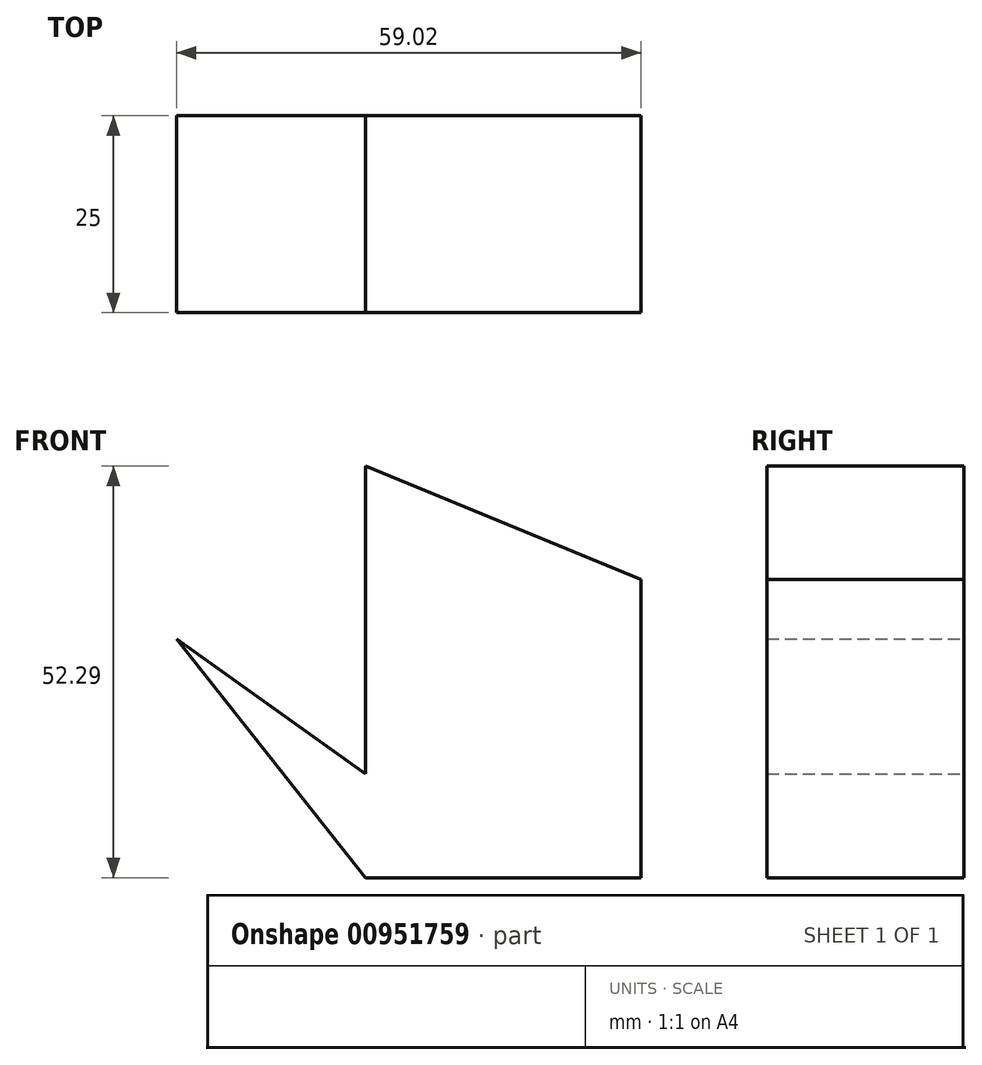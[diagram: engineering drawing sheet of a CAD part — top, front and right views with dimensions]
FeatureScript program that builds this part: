
annotation { "Feature Type Name" : "Feature", "Feature Type Description" : "" }
export const myFeature = defineFeature(function(context is Context, id is Id, definition is map)
    precondition{}
    {
        {
            var Q0;
            Q0=qCreatedBy(makeId("Front.planeOp"),FACE);
            var sketch = newSketch(context, id + "F0", { "sketchPlane" : qUnion([Q0])});
            skLineSegment(sketch, "E0", {"start": v(0, 14) * mm, "end": v(35, 14) * mm});
            skLineSegment(sketch, "E1", {"start": v(35, 14) * mm, "end": v(35, 51.88) * mm});
            skLineSegment(sketch, "E2", {"start": v(35, 51.88) * mm, "end": v(0, 66.3) * mm});
            skLineSegment(sketch, "E3", {"start": v(0, 66.3) * mm, "end": v(0, 27.18) * mm});
            skLineSegment(sketch, "E4", {"start": v(0, 27.18) * mm, "end": v(-24.02, 44.33) * mm});
            skLineSegment(sketch, "E5", {"start": v(-24.02, 44.33) * mm, "end": v(0, 14) * mm});
            skSolve(sketch);
        }
        {
            var Q0;
            Q0=makeQuery(id+"F0.imprint","IMPRINT",FACE,{"disambiguationData":[TD([[makeQuery(id+"F0.imprint","IMPRINT",EDGE,{"derivedFrom":sQuery(id+"F0.wireOp",EDGE,"E0")}),1.0]])]});
            extrude(context, id + "F1", {"entities" : qUnion([Q0]), "depth" : 25 * mm, "offsetDistance" : 25 * mm});
        }
    });
